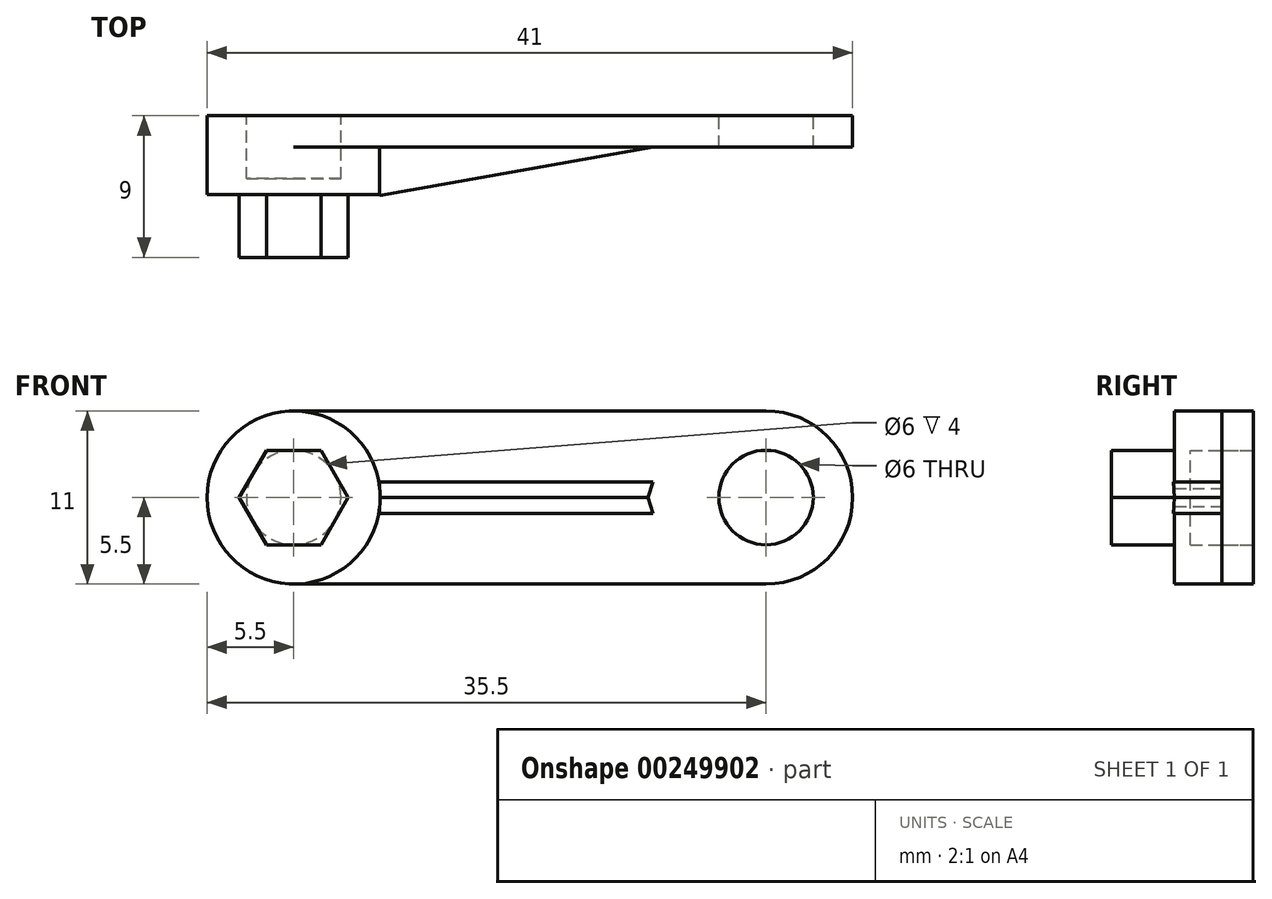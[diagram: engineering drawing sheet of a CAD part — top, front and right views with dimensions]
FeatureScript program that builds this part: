
annotation { "Feature Type Name" : "Feature", "Feature Type Description" : "" }
export const myFeature = defineFeature(function(context is Context, id is Id, definition is map)
    precondition{}
    {
        {
            var Q0;
            Q0=qCreatedBy(makeId("Front.planeOp"),FACE);
            var sketch = newSketch(context, id + "F0", { "sketchPlane" : qUnion([Q0])});
            skArc(sketch, "E0", {"start": v(-15, 5.5) * mm, "mid": v(-20.5, 0) * mm, "end": v(-15, -5.5) * mm});
            skArc(sketch, "E1", {"start": v(15, -5.5) * mm, "mid": v(20.5, 0) * mm, "end": v(15, 5.5) * mm});
            skCircle(sketch, "E2", {"center": v(-15, 0) * mm, "radius": 3 * mm});
            skCircle(sketch, "E3", {"center": v(15, 0) * mm, "radius": 3 * mm});
            skLineSegment(sketch, "E4", {"start": v(-15, 5.5) * mm, "end": v(15, 5.5) * mm});
            skLineSegment(sketch, "E5", {"start": v(-15, -5.5) * mm, "end": v(15, -5.5) * mm});
            skSolve(sketch);
        }
        {
            var Q0;
            Q0=makeQuery(id+"F0.imprint","IMPRINT",FACE,{"disambiguationData":[TD([[makeQuery(id+"F0.imprint","IMPRINT",EDGE,{"derivedFrom":sQuery(id+"F0.wireOp",EDGE,"E0")}),1.0]])]});
            extrude(context, id + "F1", {"entities" : qUnion([Q0]), "depth" : 2 * mm});
        }
        {
            var Q0;
            Q0=makeQuery(id+"F1.opExtrude","CAP_FACE",FACE,{"disambiguationData":[OSD([sQuery(id+"F0.wireOp",EDGE,"E0"),sQuery(id+"F0.wireOp",EDGE,"E1"),sQuery(id+"F0.wireOp",EDGE,"E2"),sQuery(id+"F0.wireOp",EDGE,"E3"),sQuery(id+"F0.wireOp",EDGE,"E4"),sQuery(id+"F0.wireOp",EDGE,"E5")])],"isStart":false});
            var sketch = newSketch(context, id + "F2", { "sketchPlane" : qUnion([Q0])});
            skCircle(sketch, "E6", {"center": v(-15, 0) * mm, "radius": 5.5 * mm});
            skCircle(sketch, "E7.0", {"center": v(-15, 0) * mm, "radius": 3 * mm});
            skSolve(sketch);
        }
        {
            var Q0;
            Q0=makeQuery(id+"F2.imprint","IMPRINT",FACE,{"disambiguationData":[TD([[makeQuery(id+"F2.imprint","IMPRINT",EDGE,{"derivedFrom":sQuery(id+"F2.wireOp",EDGE,"E7.0")}),-1.0]])]});
            extrude(context, id + "F3", {"entities" : qUnion([Q0]), "operationType" : NewBodyOperationType.ADD, "depth" : 2 * mm});
        }
        {
            var Q0;
            Q0=makeQuery(id+"F3.opExtrude","CAP_FACE",FACE,{"disambiguationData":[OSD([sQuery(id+"F2.wireOp",EDGE,"E6"),sQuery(id+"F2.wireOp",EDGE,"E7.0")])],"isStart":false});
            var sketch = newSketch(context, id + "F4", { "sketchPlane" : qUnion([Q0])});
            skCircle(sketch, "E8.0", {"center": v(-15, 0) * mm, "radius": 5.5 * mm});
            skCircle(sketch, "E9.0", {"center": v(-15, 0) * mm, "radius": 3 * mm});
            skSolve(sketch);
        }
        {
            var Q0;
            Q0=makeQuery(id+"F4.imprint","IMPRINT",FACE,{"disambiguationData":[TD([[makeQuery(id+"F4.imprint","IMPRINT",EDGE,{"derivedFrom":sQuery(id+"F4.wireOp",EDGE,"E8.0")}),1.0]])]});
            var Q1;
            Q1=makeQuery(id+"F4.imprint","IMPRINT",FACE,{"disambiguationData":[TD([[makeQuery(id+"F4.imprint","IMPRINT",EDGE,{"derivedFrom":sQuery(id+"F4.wireOp",EDGE,"E9.0")}),1.0]])]});
            extrude(context, id + "F5", {"entities" : qUnion([Q0, Q1]), "operationType" : NewBodyOperationType.ADD, "depth" : 1 * mm});
        }
        {
            var Q0;
            Q0=makeQuery(id+"F5.opExtrude","CAP_FACE",FACE,{"disambiguationData":[OSD([sQuery(id+"F4.wireOp",EDGE,"E8.0")])],"isStart":false});
            var sketch = newSketch(context, id + "F6", { "sketchPlane" : qUnion([Q0])});
            skCircle(sketch, "E10.0", {"center": v(-15, 0) * mm, "radius": 3 * mm});
            skLineSegment(sketch, "E11.0", {"start": v(-16.73, 3) * mm, "end": v(-13.27, 3) * mm});
            skLineSegment(sketch, "E11.1", {"start": v(-13.27, 3) * mm, "end": v(-11.54, 0) * mm});
            skLineSegment(sketch, "E11.2", {"start": v(-11.54, 0) * mm, "end": v(-13.27, -3) * mm});
            skLineSegment(sketch, "E11.3", {"start": v(-13.27, -3) * mm, "end": v(-16.73, -3) * mm});
            skLineSegment(sketch, "E11.4", {"start": v(-16.73, -3) * mm, "end": v(-18.46, 0) * mm});
            skLineSegment(sketch, "E11.5", {"start": v(-18.46, 0) * mm, "end": v(-16.73, 3) * mm});
            skPoint(sketch, "E11.0.midPoint", {"position": v(-15, 3) * mm});
            skSolve(sketch);
        }
        {
            var Q0;
            {var subQ0=sQuery(id+"F6.wireOp",EDGE,"E11.2");var subQ1=sQuery(id+"F6.wireOp",EDGE,"E10.0");var subQ2=makeQuery(id+"F6.imprint","INTERSECT",VERTEX,{"derivedFrom":[subQ1,subQ0]});Q0=makeQuery(id+"F6.imprint","IMPRINT",FACE,{"disambiguationData":[TD([[makeQuery(id+"F6.imprint","IMPRINT",EDGE,{"disambiguationData":[TD([[subQ2,1.0]])],"derivedFrom":subQ1}),-1.0]])]});}
            var Q1;
            {var subQ0=sQuery(id+"F6.wireOp",EDGE,"E11.2");var subQ1=sQuery(id+"F6.wireOp",EDGE,"E10.0");var subQ2=makeQuery(id+"F6.imprint","INTERSECT",VERTEX,{"derivedFrom":[subQ1,subQ0]});Q1=makeQuery(id+"F6.imprint","IMPRINT",FACE,{"disambiguationData":[TD([[makeQuery(id+"F6.imprint","IMPRINT",EDGE,{"disambiguationData":[TD([[subQ2,-1.0]])],"derivedFrom":subQ1}),-1.0]])]});}
            var Q2;
            {var subQ0=sQuery(id+"F6.wireOp",EDGE,"E11.1");var subQ1=sQuery(id+"F6.wireOp",EDGE,"E10.0");var subQ2=makeQuery(id+"F6.imprint","INTERSECT",VERTEX,{"derivedFrom":[subQ1,subQ0]});Q2=makeQuery(id+"F6.imprint","IMPRINT",FACE,{"disambiguationData":[TD([[makeQuery(id+"F6.imprint","IMPRINT",EDGE,{"disambiguationData":[TD([[subQ2,-1.0]])],"derivedFrom":subQ1}),-1.0]])]});}
            var Q3;
            {var subQ0=sQuery(id+"F6.wireOp",EDGE,"E11.5");var subQ1=sQuery(id+"F6.wireOp",EDGE,"E10.0");var subQ2=makeQuery(id+"F6.imprint","INTERSECT",VERTEX,{"derivedFrom":[subQ1,subQ0]});Q3=makeQuery(id+"F6.imprint","IMPRINT",FACE,{"disambiguationData":[TD([[makeQuery(id+"F6.imprint","IMPRINT",EDGE,{"disambiguationData":[TD([[subQ2,-1.0]])],"derivedFrom":subQ1}),-1.0]])]});}
            var Q4;
            {var subQ0=sQuery(id+"F6.wireOp",EDGE,"E11.3");var subQ1=sQuery(id+"F6.wireOp",EDGE,"E10.0");var subQ2=makeQuery(id+"F6.imprint","INTERSECT",VERTEX,{"derivedFrom":[subQ1,subQ0]});Q4=makeQuery(id+"F6.imprint","IMPRINT",FACE,{"disambiguationData":[TD([[makeQuery(id+"F6.imprint","IMPRINT",EDGE,{"disambiguationData":[TD([[subQ2,1.0]])],"derivedFrom":subQ1}),-1.0]])]});}
            var Q5;
            {var subQ0=sQuery(id+"F6.wireOp",EDGE,"E10.0");var subQ5=makeQuery(id+"F6.imprint","INTERSECT",VERTEX,{"derivedFrom":[subQ0,sQuery(id+"F6.wireOp",EDGE,"E11.2")]});Q5=makeQuery(id+"F6.imprint","IMPRINT",FACE,{"disambiguationData":[TD([[makeQuery(id+"F6.imprint","IMPRINT",EDGE,{"disambiguationData":[TD([[subQ5,1.0]])],"derivedFrom":subQ0}),1.0]])]});}
            var Q6;
            {var subQ0=sQuery(id+"F6.wireOp",EDGE,"E11.0");var subQ1=sQuery(id+"F6.wireOp",EDGE,"E10.0");var subQ2=makeQuery(id+"F6.imprint","INTERSECT",VERTEX,{"derivedFrom":[subQ1,subQ0]});Q6=makeQuery(id+"F6.imprint","IMPRINT",FACE,{"disambiguationData":[TD([[makeQuery(id+"F6.imprint","IMPRINT",EDGE,{"disambiguationData":[TD([[subQ2,-1.0]])],"derivedFrom":subQ1}),-1.0]])]});}
            extrude(context, id + "F7", {"entities" : qUnion([Q0, Q1, Q2, Q3, Q4, Q5, Q6]), "operationType" : NewBodyOperationType.ADD, "depth" : 4 * mm});
        }
        {
            var Q0;
            Q0=makeQuery(id+"F7.opExtrude","SWEPT_FACE",FACE,{"disambiguationData":[OSD([sQuery(id+"F6.wireOp",EDGE,"E11.3")])]});
            cPlane(context, id + "F8", {"entities" : qUnion([Q0]), "cplaneType" : CPlaneType.OFFSET, "offset" : 3 * mm, "oppositeDirection" : true, "width" : 150 * mm, "height" : 150 * mm});
        }
        {
            var Q0;
            Q0=qCreatedBy(id+"F8.planeOp",FACE);
            var sketch = newSketch(context, id + "F9", { "sketchPlane" : qUnion([Q0])});
            skLineSegment(sketch, "E12", {"start": v(-9.5, 5) * mm, "end": v(7.51, 2) * mm});
            skLineSegment(sketch, "E13.0", {"start": v(-20.5, 5) * mm, "end": v(-9.5, 5) * mm});
            skLineSegment(sketch, "E14", {"start": v(-9.5, 5) * mm, "end": v(-9.5, 2) * mm});
            skLineSegment(sketch, "E15.0", {"start": v(-9.5, 2) * mm, "end": v(15, 2) * mm});
            skPoint(sketch, "E16.orphan", {"position": v(-15, 2) * mm});
            skSolve(sketch);
        }
        {
            var Q0;
            Q0 = qSketchRegion(id + "F9", true);
            extrude(context, id + "F10", {"entities" : qUnion([Q0]), "operationType" : NewBodyOperationType.ADD, "endBound" : BoundingType.SYMMETRIC, "depth" : 2 * mm, "hasDraft" : true, "draftAngle" : 3 * degree});
        }
    });
